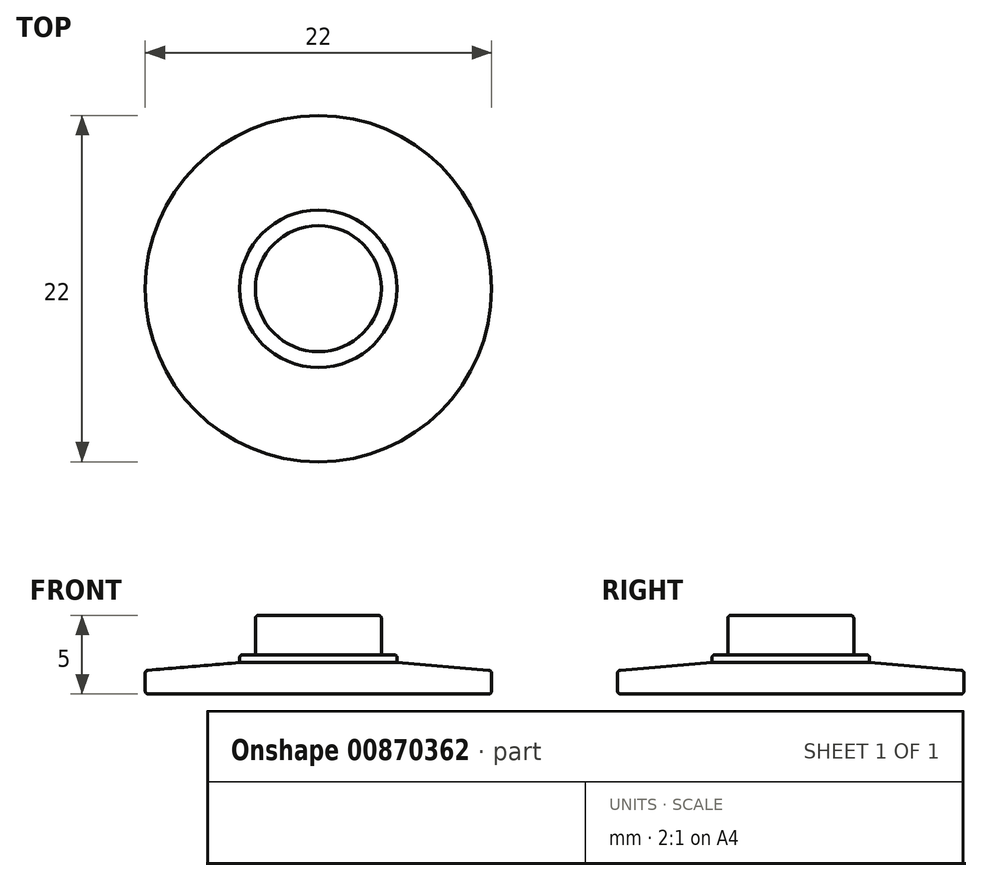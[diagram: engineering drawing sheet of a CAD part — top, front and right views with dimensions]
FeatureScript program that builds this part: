
annotation { "Feature Type Name" : "Feature", "Feature Type Description" : "" }
export const myFeature = defineFeature(function(context is Context, id is Id, definition is map)
    precondition{}
    {
        {
            var Q0;
            Q0=qCreatedBy(makeId("Top.planeOp"),FACE);
            var sketch = newSketch(context, id + "F0", { "sketchPlane" : qUnion([Q0])});
            skCircle(sketch, "E0", {"center": v(0, 0) * mm, "radius": 11 * mm});
            skSolve(sketch);
        }
        {
            var Q0;
            Q0=qSketchRegion(id+"F0",true);
            extrude(context, id + "F1", {"entities" : qUnion([Q0]), "depth" : 2 * mm, "offsetDistance" : 25 * mm});
        }
        {
            var Q0;
            Q0=makeQuery(id+"F1.opExtrude","CAP_FACE",FACE,{"disambiguationData":[OSD([sQuery(id+"F0.wireOp",EDGE,"E0")])],"isStart":false});
            var sketch = newSketch(context, id + "F2", { "sketchPlane" : qUnion([Q0])});
            skCircle(sketch, "E1", {"center": v(0, 0) * mm, "radius": 5 * mm});
            skSolve(sketch);
        }
        {
            var Q0;
            Q0=qSketchRegion(id+"F2",true);
            extrude(context, id + "F3", {"entities" : qUnion([Q0]), "operationType" : NewBodyOperationType.ADD, "depth" : 0.5 * mm, "offsetDistance" : 25 * mm});
        }
        {
            var Q0;
            Q0=makeQuery(id+"F3.opExtrude","CAP_FACE",FACE,{"disambiguationData":[OSD([sQuery(id+"F2.wireOp",EDGE,"E1")])],"isStart":false});
            var sketch = newSketch(context, id + "F4", { "sketchPlane" : qUnion([Q0])});
            skCircle(sketch, "E2", {"center": v(0, 0) * mm, "radius": 4 * mm});
            skSolve(sketch);
        }
        {
            var Q0;
            Q0=qSketchRegion(id+"F4",true);
            extrude(context, id + "F5", {"entities" : qUnion([Q0]), "operationType" : NewBodyOperationType.ADD, "depth" : 2.5 * mm, "offsetDistance" : 25 * mm});
        }
        {
            var Q0;
            Q0=makeQuery(id+"F1.opExtrude","CAP_EDGE",EDGE,{"disambiguationData":[OSD([sQuery(id+"F0.wireOp",EDGE,"E0")])],"isStart":false});
            chamfer(context, id + "F6", {"entities" : qUnion([Q0]), "chamferType" : ChamferType.TWO_OFFSETS, "width1" : 6 * mm, "oppositeDirection" : false, "width2" : 0.5 * mm, "tangentPropagation" : true});
        }
        {
            var Q0;
            Q0=makeQuery(id+"F5.opExtrude","CAP_EDGE",EDGE,{"disambiguationData":[OSD([sQuery(id+"F4.wireOp",EDGE,"E2")])],"isStart":false});
            var Q1;
            Q1=makeQuery(id+"F3.opExtrude","CAP_EDGE",EDGE,{"disambiguationData":[OSD([sQuery(id+"F2.wireOp",EDGE,"E1")])],"isStart":false});
            var Q2;
            Q2=makeQuery(id+"F1.opExtrude","CAP_EDGE",EDGE,{"disambiguationData":[OSD([sQuery(id+"F0.wireOp",EDGE,"E0")])],"isStart":true});
            var Q3;
            {var subQ0=sQuery(id+"F0.wireOp",EDGE,"E0");Q3=makeQuery(id+"F6.opChamfer","BLEND_EDGE",EDGE,{"blendedFrom":[makeQuery(id+"F1.opExtrude","CAP_EDGE",EDGE,{"disambiguationData":[OSD([subQ0])],"isStart":false}),makeQuery(id+"F1.opExtrude","SWEPT_FACE",FACE,{"disambiguationData":[OSD([subQ0])]})],"blendedInto":[makeQuery(id+"F1.opExtrude","SWEPT_FACE",FACE,{"disambiguationData":[OSD([subQ0])]})]});}
            fillet(context, id + "F7", {"entities" : qUnion([Q0, Q1, Q2, Q3]), "radius" : 0.2 * mm, "tangentPropagation" : true, "allowEdgeOverflow" : false});
        }
    });
